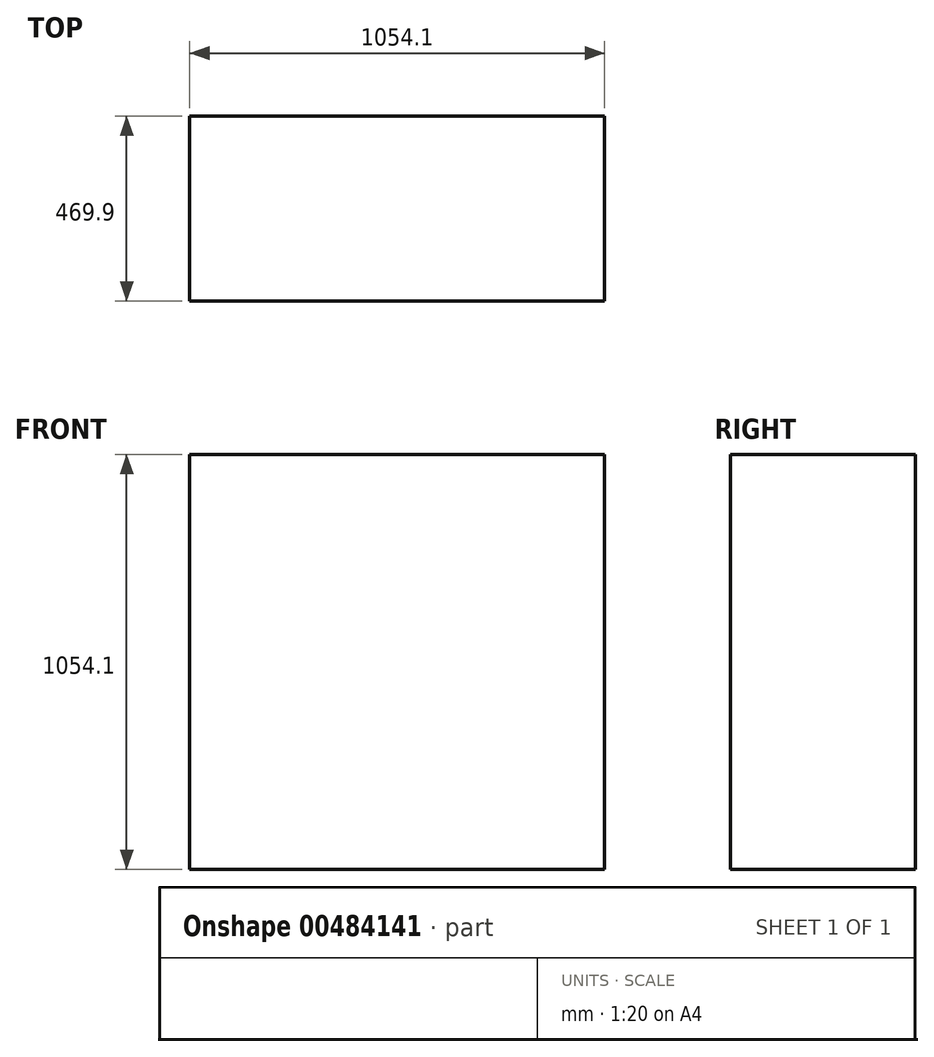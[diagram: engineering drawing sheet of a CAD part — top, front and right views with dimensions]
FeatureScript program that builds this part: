
annotation { "Feature Type Name" : "Feature", "Feature Type Description" : "" }
export const myFeature = defineFeature(function(context is Context, id is Id, definition is map)
    precondition{}
    {
        {
            var Q0;
            Q0=qCreatedBy(makeId("Front.planeOp"),FACE);
            var sketch = newSketch(context, id + "F0", { "sketchPlane" : qUnion([Q0])});
            skLineSegment(sketch, "E0.bottom", {"start": v(0, 0) * mm, "end": v(1054.1, 0) * mm});
            skLineSegment(sketch, "E0.top", {"start": v(0, 1054.1) * mm, "end": v(1054.1, 1054.1) * mm});
            skLineSegment(sketch, "E0.left", {"start": v(0, 0) * mm, "end": v(0, 1054.1) * mm});
            skLineSegment(sketch, "E0.right", {"start": v(1054.1, 0) * mm, "end": v(1054.1, 1054.1) * mm});
            skSolve(sketch);
        }
        {
            var Q0;
            Q0 = qSketchRegion(id + "F0", true);
            extrude(context, id + "F1", {"entities" : qUnion([Q0]), "depth" : 469.9 * mm, "offsetDistance" : 25.4 * mm});
        }
    });
